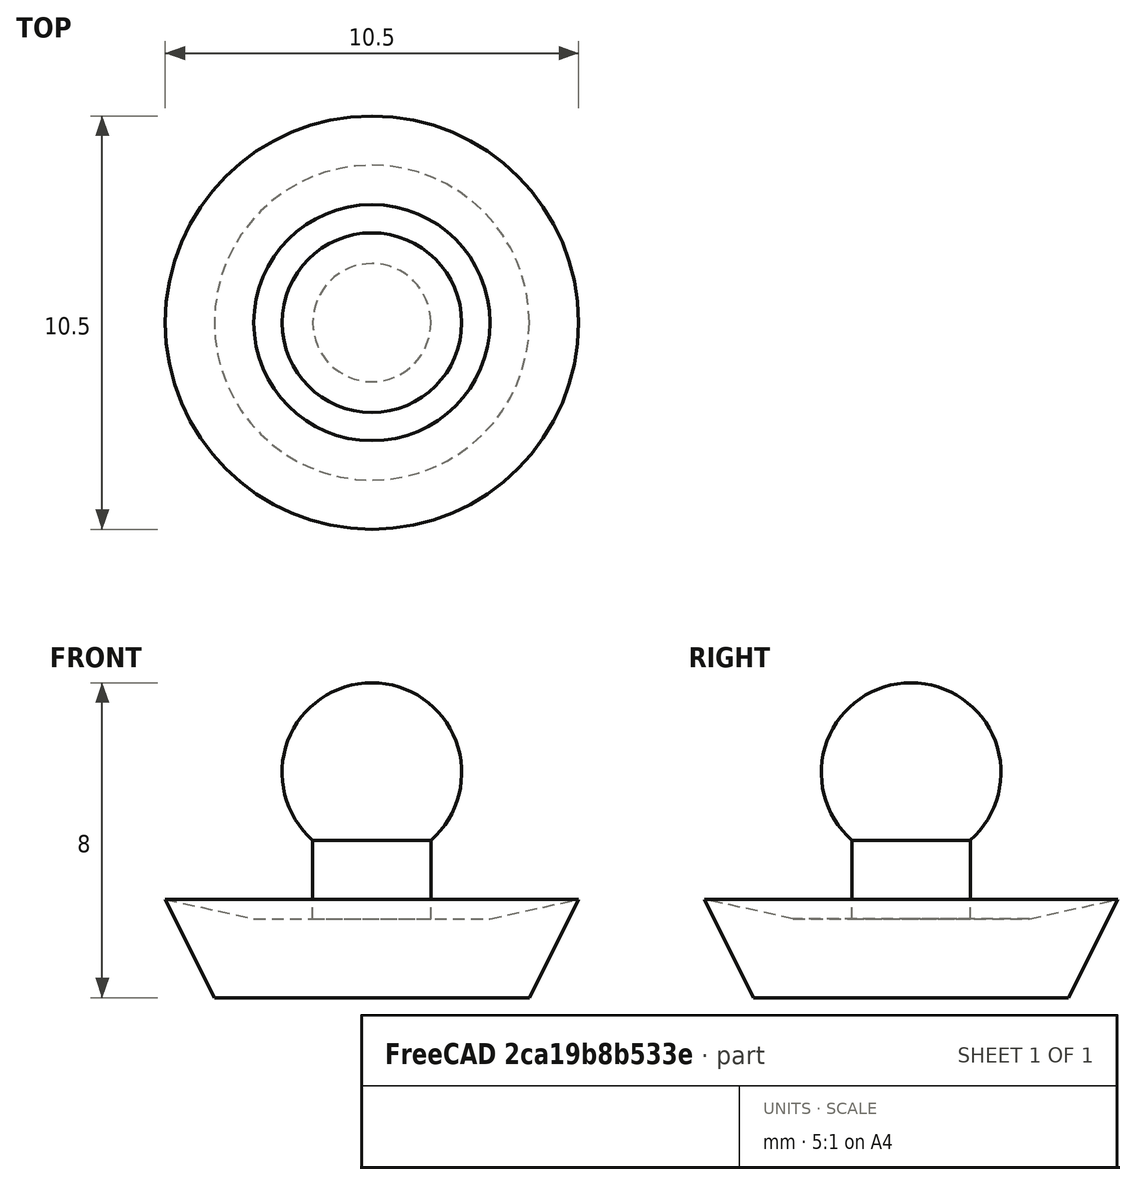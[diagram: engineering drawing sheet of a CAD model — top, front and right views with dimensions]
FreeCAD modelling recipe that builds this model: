
FCSTD DOCUMENT  (FreeCAD 0.21R33771 (Git))
Label: territory-marker
License: All rights reserved
LicenseURL: http://en.wikipedia.org/wiki/All_rights_reserved
objects: Sketcher::SketchObject×1, PartDesign::Revolution×1, PartDesign::Body×1
note: 4 computed .brp shape members not serialized (recipe doc carries the construction recipe); baked Part::Feature solids carry a one-line shape summary decoded from their .brp

FEATURE [Sketcher::SketchObject] Sketch
  FullyConstrained = true
  MapMode = 5
  Placement = pos=(0,0,0) rot=(1,0,0;1.5708rad)
  Support = -> [XZ_Plane]
  sketch-geometry (7):
    g0: LineSegment StartX=0 StartY=0 StartZ=0 EndX=-4 EndY=0 EndZ=0
    g1: LineSegment StartX=-4 StartY=0 StartZ=0 EndX=-5.25 EndY=2.5 EndZ=0
    g2: LineSegment StartX=-5.25 StartY=2.5 StartZ=0 EndX=-3 EndY=2 EndZ=0
    g3: LineSegment StartX=-3 StartY=2 StartZ=0 EndX=-1.5 EndY=2 EndZ=0
    g4: LineSegment StartX=1e-16 StartY=8 StartZ=0 EndX=0 EndY=0 EndZ=0
    g5: ArcOfCircle CenterX=0 CenterY=5.71875 CenterZ=0 NormalX=0 NormalY=0 NormalZ=1 AngleXU=0 Radius=2.28125 StartAngle=1.5708 EndAngle=3.99485
    g6: LineSegment StartX=-1.5 StartY=2 StartZ=0 EndX=-1.5 EndY=4 EndZ=0
  constraints (21):
    c: Coincident(g0,g-1)
    c: PointOnObject(g0,g-1)
    c: Coincident(g1,g0)
    c: Coincident(g2,g1)
    c: Coincident(g3,g2)
    c: Horizontal(g3)
    c: Coincident(g4,g0)
    c: Coincident(g6,g3)
    c: PointOnObject(g5,g-2)
    c: Coincident(g4,g5)
    c: PointOnObject(g5,g-2)
    c: Coincident(g5,g6)
    c: DistanceX(g0,g0) = 4
    c: DistanceY(g4,g4) = 8
    c: Distance(g1,g4) = 5.25
    c: Angle(g6,g3) = 1.5708
    c: DistanceY(g-1,g1) = 2.5
    c: Distance(g5,g4) = 1.5
    c: DistanceY(g-1,g3) = 2
    c: DistanceX(g-2,g2) = -3
    c: DistanceY(g-1,g5) = 4
FEATURE [PartDesign::Revolution] Revolution
  Angle = 360
  Axis = (0,2e-16,1)
  Base = (0,0,0)
  Placement = pos=(0,0,0) rot=(1,0,0;1.5708rad)
  Profile = -> Sketch
  ReferenceAxis = -> Sketch [V_Axis]
FEATURE [PartDesign::Body] Body
  Group = -> [Sketch,Revolution]
  Origin = -> Origin
  Tip = -> Revolution
